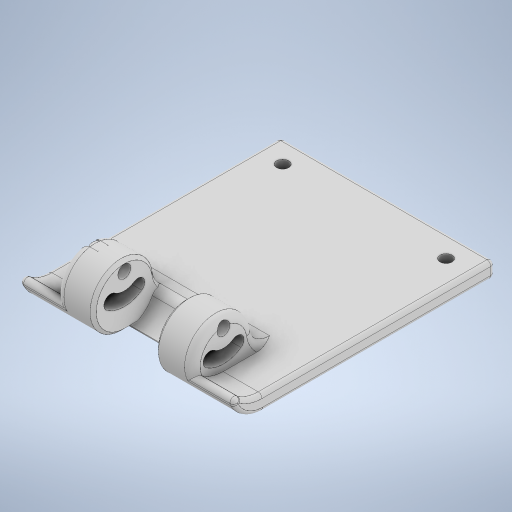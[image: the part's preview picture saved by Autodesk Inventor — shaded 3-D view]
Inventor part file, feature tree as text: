
AUTODESK INVENTOR PART (.ipt)
format: ipt  version: 2023 (Build 270158030, 158C)  size: 399,360 bytes
history: native  units: mm
features: other x4, chamfer x3
ambient origin geometry x8: Origin, YZ Plane, XZ Plane, XY Plane, X Axis, Y Axis, Z Axis, Center Point
bodies: Body1 (feature_tree)
feature tree (7):
  other  "glowbot-sensor-bumper.ipt"
  chamfer  "Chamfer1"  Distance=10.0mm
  chamfer  "Chamfer2"  Distance=2.0mm Angle=45.0deg
  chamfer  "Chamfer3"  Distance=0.8mm Angle=45.0deg
  other  "hoz-mount::glowbot-sensor-bumper.ipt"
  other  "TaggingFeature1"
  other  "hoz-mount"
